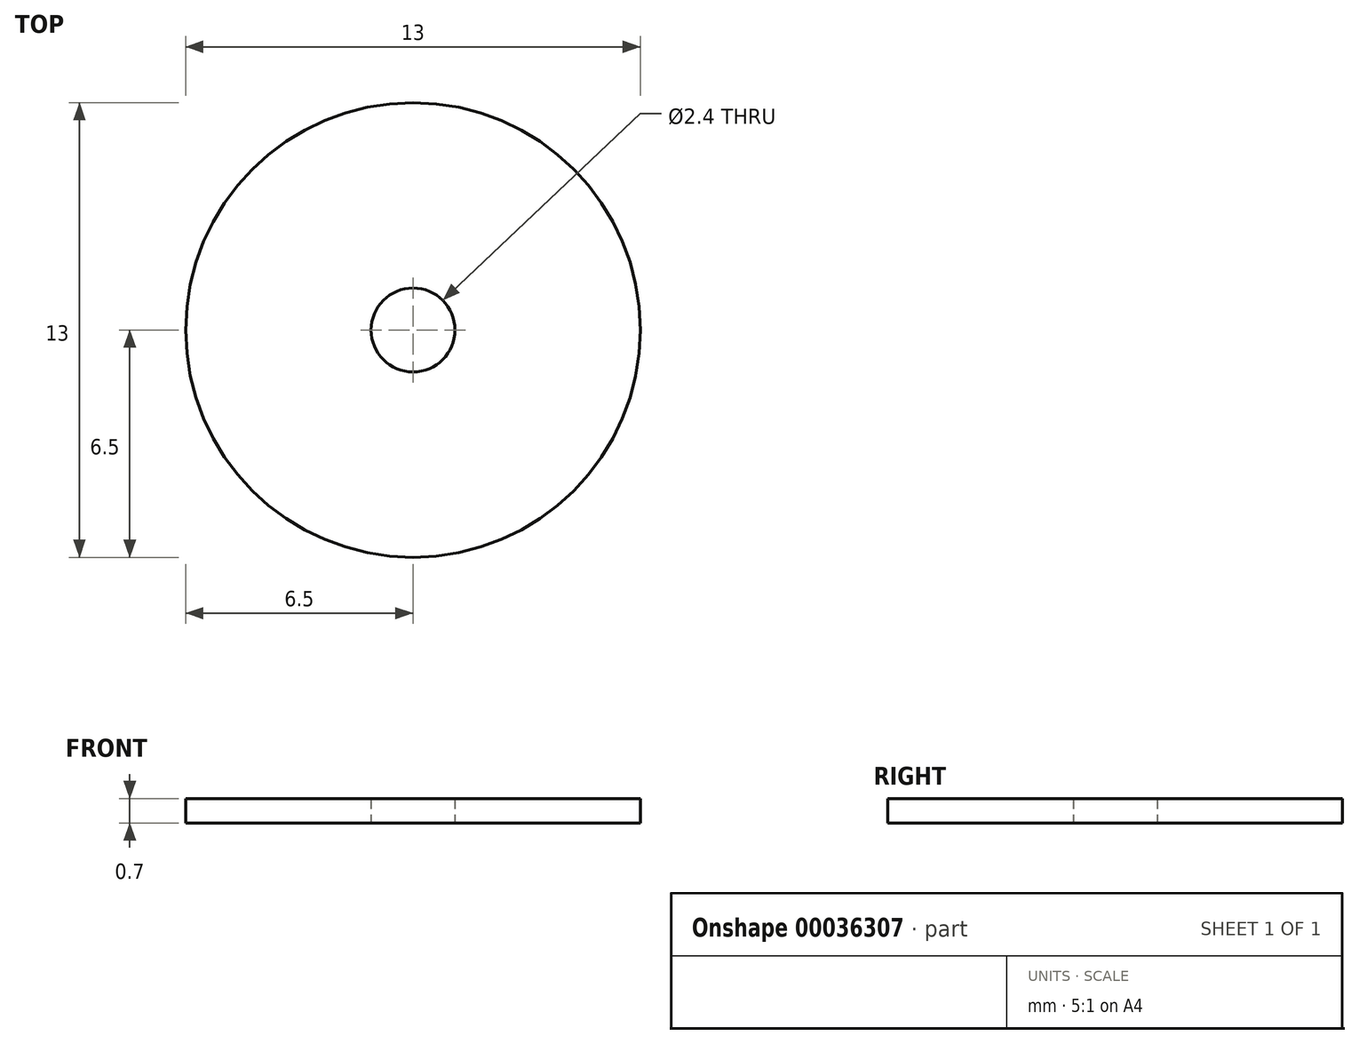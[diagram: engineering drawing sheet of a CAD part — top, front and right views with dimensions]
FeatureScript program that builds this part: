
annotation { "Feature Type Name" : "Feature", "Feature Type Description" : "" }
export const myFeature = defineFeature(function(context is Context, id is Id, definition is map)
    precondition{}
    {
        {
            var Q0;
            Q0=qCreatedBy(makeId("Top.planeOp"),FACE);
            var sketch = newSketch(context, id + "F0", { "sketchPlane" : qUnion([Q0])});
            skCircle(sketch, "E0", {"center": v(0, 0) * mm, "radius": 6.5 * mm});
            skCircle(sketch, "E1", {"center": v(0, 0) * mm, "radius": 1.2 * mm});
            skSolve(sketch);
        }
        {
            var Q0;
            Q0=makeQuery(id+"F0.imprint","IMPRINT",FACE,{"disambiguationData":[TD([[makeQuery(id+"F0.imprint","IMPRINT",EDGE,{"derivedFrom":sQuery(id+"F0.wireOp",EDGE,"E0")}),1.0]])]});
            extrude(context, id + "F1", {"entities" : qUnion([Q0]), "depth" : 0.7 * mm});
        }
    });
